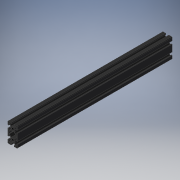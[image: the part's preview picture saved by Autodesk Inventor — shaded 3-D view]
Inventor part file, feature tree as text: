
AUTODESK INVENTOR PART (.ipt)
format: ipt  version: 2019 (Build 230136000, 136)  size: 295,936 bytes
history: native  units: mm
features: other x7, sketch x4, hole x3, pattern_linear x3, extrude x1
ambient origin geometry x8: Origin, YZ Plane, XZ Plane, XY Plane, X Axis, Y Axis, Z Axis, Center Point
bodies: Solid1 (feature_tree)
feature tree (18):
  extrude  "Extrusion1"  Depth=20.0mm TaperAngle=0.0deg
  hole  "Hole1"  [1 undecoded]
  pattern_linear  "Rectangular Pattern1"  Count1=2 Spacing1=10.0mm
  hole  "Hole2"  [1 undecoded]
  pattern_linear  "Rectangular Pattern2"  [2 undecoded]
  hole  "Hole3"  [1 undecoded]
  pattern_linear  "Rectangular Pattern3"  [2 undecoded]
  other  "C1_XY"
  other  "C1_YZ"
  other  "C1_ZX"
  other  "C1_X"
  other  "C1_Y"
  other  "C1_Z"
  other  "C1_Center"
  sketch  "Sketch_1"  dims[d0=320.0mm d1=0.0mm]
  sketch  "Sketch2"  dims[d2=4.134mm d3=15.0mm d4=5.0mm d5=2.0mm d6=90.0deg d7=15.0mm d8=0.0mm d9=20.0mm d11=20.0mm d12=10.0mm d14=0.0mm]
  sketch  "Sketch3"  dims[d15=4.134mm d16=15.0mm d17=5.0mm d18=2.0mm d19=90.0deg d20=15.0mm d21=0.0mm d22=20.0mm d24=20.0mm d25=10.0mm d27=0.0mm]
  sketch  "Sketch4"  dims[d28=4.2mm d29=6.0mm d30=4.0mm d31=2.0mm d32=90.0deg d33=290.0mm d34=0.0mm d35=20.0mm d37=20.0mm d38=10.0mm d40=0.0mm d41=0.0mm]
note: 7 required parameter values undecoded (feature->parameter linkage not recoverable at this tier; creation-order binding heuristic only, values carry confidence <= 0.55)
